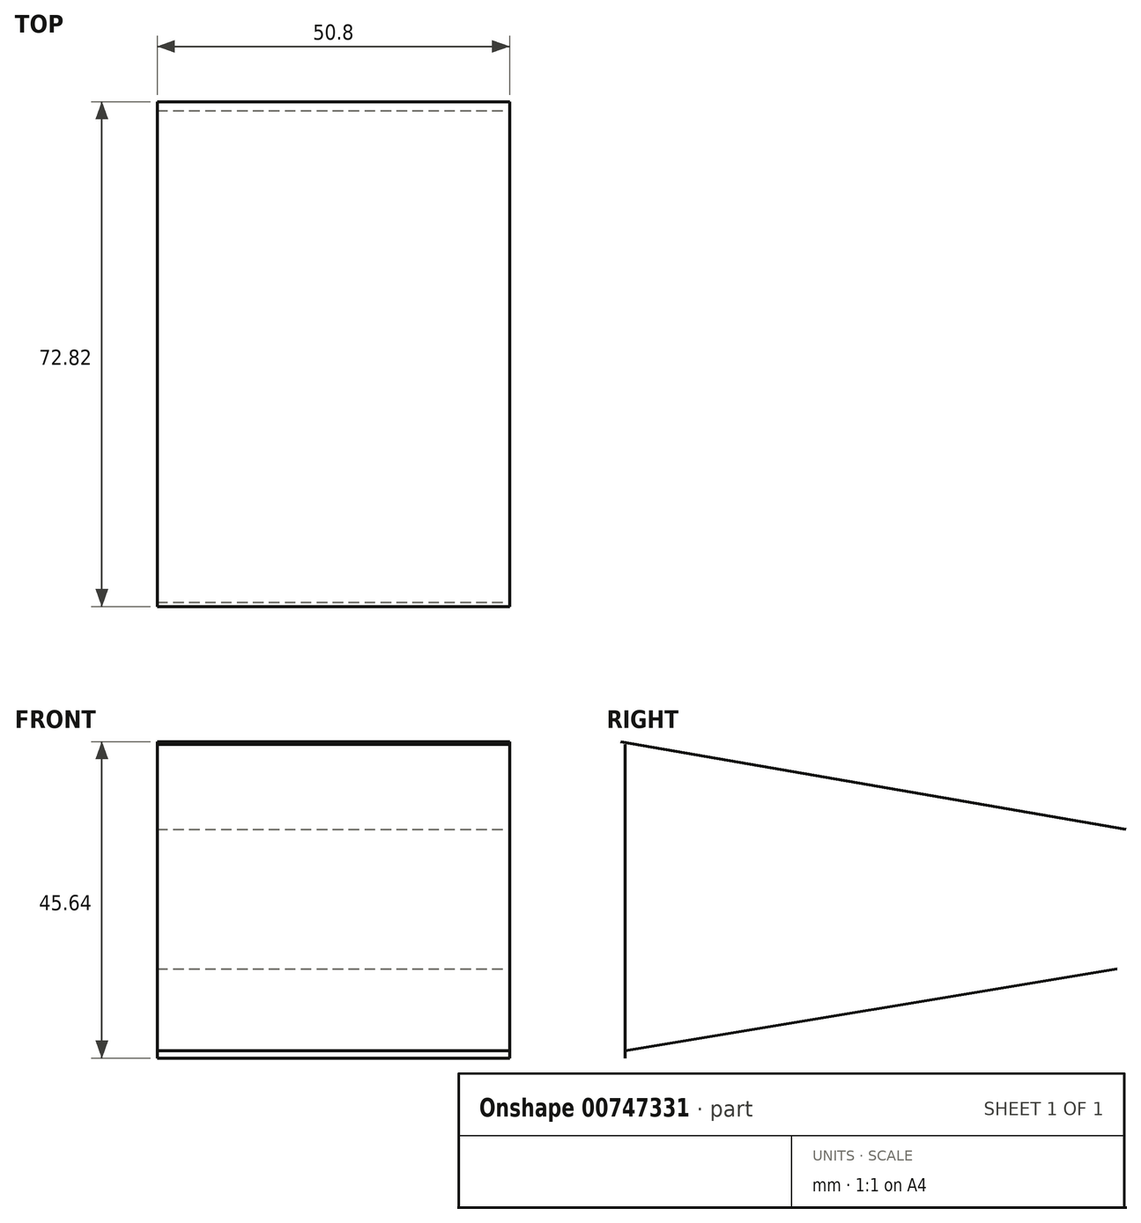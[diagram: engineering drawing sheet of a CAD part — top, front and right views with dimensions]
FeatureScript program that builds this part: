
annotation { "Feature Type Name" : "Feature", "Feature Type Description" : "" }
export const myFeature = defineFeature(function(context is Context, id is Id, definition is map)
    precondition{}
    {
        {
            var Q0;
            Q0=qCreatedBy(makeId("Right.planeOp"),FACE);
            var sketch = newSketch(context, id + "F0", { "sketchPlane" : qUnion([Q0])});
            skLineSegment(sketch, "E0", {"start": v(-29.46, 32.78) * mm, "end": v(43.36, 20.12) * mm});
            skSolve(sketch);
        }
        {
            var Q0;
            Q0=qCreatedBy(makeId("Right.planeOp"),FACE);
            var sketch = newSketch(context, id + "F1", { "sketchPlane" : qUnion([Q0])});
            skLineSegment(sketch, "E1", {"start": v(-28.84, -11.83) * mm, "end": v(42.11, 0) * mm});
            skLineSegment(sketch, "E2", {"start": v(42.11, 0) * mm, "end": v(42.11, 19.92) * mm});
            skSolve(sketch);
        }
        {
            var Q0;
            Q0=qCreatedBy(makeId("Right.planeOp"),FACE);
            var sketch = newSketch(context, id + "F2", { "sketchPlane" : qUnion([Q0])});
            skLineSegment(sketch, "E3", {"start": v(-28.84, 32.36) * mm, "end": v(-28.84, -12.86) * mm});
            skSolve(sketch);
        }
        {
            var Q0;
            Q0=sQuery(id+"F0.wireOp",EDGE,"E0");
            extrude(context, id + "F3", {"bodyType" : ToolBodyType.SURFACE, "surfaceEntities" : qUnion([Q0]), "depth" : 50.8 * mm, "offsetDistance" : 25.4 * mm});
        }
        {
            var Q0;
            Q0=sQuery(id+"F2.wireOp",EDGE,"E3");
            extrude(context, id + "F4", {"bodyType" : ToolBodyType.SURFACE, "surfaceEntities" : qUnion([Q0]), "depth" : 50.8 * mm, "offsetDistance" : 25.4 * mm});
        }
        {
            var Q0;
            Q0=sQuery(id+"F1.wireOp",EDGE,"E1");
            extrude(context, id + "F5", {"bodyType" : ToolBodyType.SURFACE, "surfaceEntities" : qUnion([Q0]), "depth" : 50.8 * mm, "offsetDistance" : 25.4 * mm});
        }
    });
